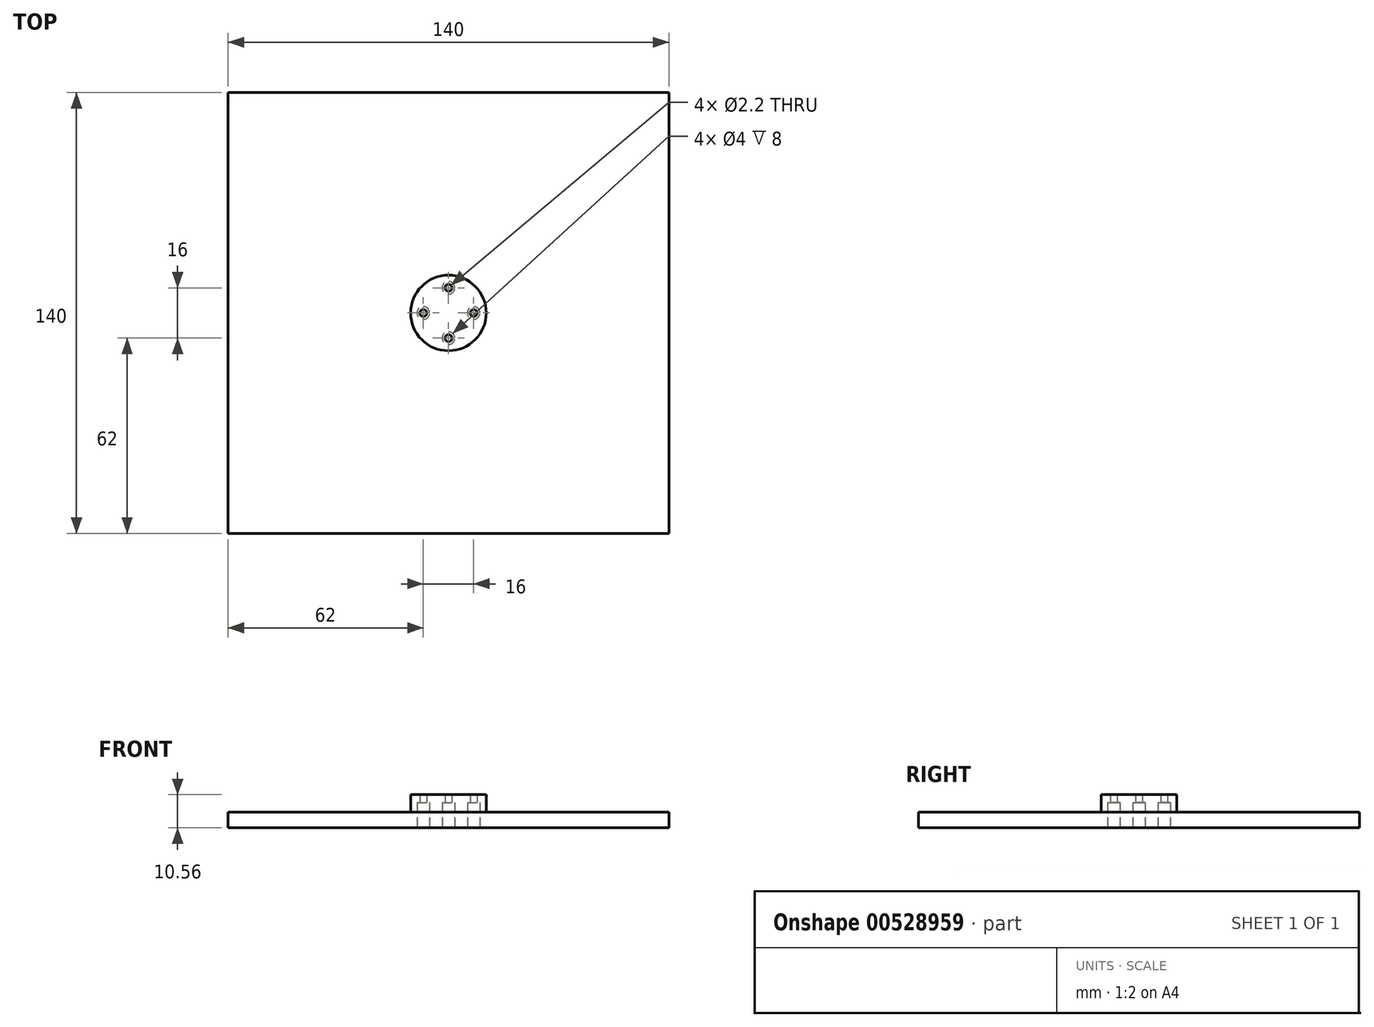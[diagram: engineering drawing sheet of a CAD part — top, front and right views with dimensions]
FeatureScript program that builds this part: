
annotation { "Feature Type Name" : "Feature", "Feature Type Description" : "" }
export const myFeature = defineFeature(function(context is Context, id is Id, definition is map)
    precondition{}
    {
        {
            var Q0;
            Q0=qCreatedBy(makeId("Top.planeOp"),FACE);
            var sketch = newSketch(context, id + "F0", { "sketchPlane" : qUnion([Q0])});
            skLineSegment(sketch, "E0.bottom", {"start": v(70, -70) * mm, "end": v(-70, -70) * mm});
            skLineSegment(sketch, "E0.top", {"start": v(70, 70) * mm, "end": v(-70, 70) * mm});
            skLineSegment(sketch, "E0.left", {"start": v(70, -70) * mm, "end": v(70, 70) * mm});
            skLineSegment(sketch, "E0.right", {"start": v(-70, -70) * mm, "end": v(-70, 70) * mm});
            skPoint(sketch, "E0.middle", {"position": v(0, 0) * mm});
            skCircle(sketch, "E1", {"center": v(0, 0) * mm, "radius": 8 * mm, "construction": true});
            skCircle(sketch, "E2", {"center": v(0, 0) * mm, "radius": 12 * mm});
            skPoint(sketch, "E3", {"position": v(0, 8) * mm});
            skPoint(sketch, "E4", {"position": v(8, 0) * mm});
            skPoint(sketch, "E5", {"position": v(0, -8) * mm});
            skPoint(sketch, "E6", {"position": v(-8, 0) * mm});
            skSolve(sketch);
        }
        {
            var Q0;
            Q0 = qSketchRegion(id + "F0", true);
            extrude(context, id + "F1", {"entities" : qUnion([Q0]), "depth" : 5 * mm, "offsetDistance" : 25 * mm});
        }
        {
            var Q0;
            Q0=makeQuery(id+"F0.imprint","IMPRINT",FACE,{"disambiguationData":[TD([[makeQuery(id+"F0.imprint","IMPRINT",EDGE,{"derivedFrom":sQuery(id+"F0.wireOp",EDGE,"mxtSTHb5-2sSW-HKk8-hwSK-mRPs5wV7HEU5")}),-1.0]])]});
            var Q1;
            Q1=makeQuery(id+"F0.imprint","IMPRINT",FACE,{"disambiguationData":[TD([[makeQuery(id+"F0.imprint","IMPRINT",EDGE,{"derivedFrom":sQuery(id+"F0.wireOp",EDGE,"E2")}),1.0]])]});
            extrude(context, id + "F2", {"entities" : qUnion([Q0, Q1]), "operationType" : NewBodyOperationType.ADD, "depth" : 10.56 * mm, "offsetDistance" : 25 * mm});
        }
        {
            var Q0;
            Q0=sQuery(id+"F0.wireOp",VERTEX,"E4");
            var Q1;
            Q1=sQuery(id+"F0.wireOp",VERTEX,"E3");
            var Q2;
            Q2=sQuery(id+"F0.wireOp",VERTEX,"E6");
            var Q3;
            Q3=sQuery(id+"F0.wireOp",VERTEX,"E5");
            var Q4;
            Q4=makeQuery(id+"F1.opExtrude","SWEPT_BODY",BODY,{"disambiguationData":[OSD([sQuery(id+"F0.wireOp",EDGE,"E0.bottom"),sQuery(id+"F0.wireOp",EDGE,"E0.top"),sQuery(id+"F0.wireOp",EDGE,"E0.left"),sQuery(id+"F0.wireOp",EDGE,"E0.right"),sQuery(id+"F0.wireOp",EDGE,"E2")])]});
            hole(context, id + "F3", {"style" : HoleStyle.C_BORE, "endStyle" : HoleEndStyle.BLIND, "oppositeDirection" : true, "holeDiameter" : 2.2 * mm, "cBoreDiameter" : 4 * mm, "cBoreDepth" : 8 * mm, "majorDiameter" : 5 * mm, "holeDepth" : 12 * mm, "isTappedThrough" : true, "tappedDepth" : 12 * mm, "tapClearance" : 3, "locations" : qUnion([Q0, Q1, Q2, Q3]), "scope" : qUnion([Q4])});
        }
    });
